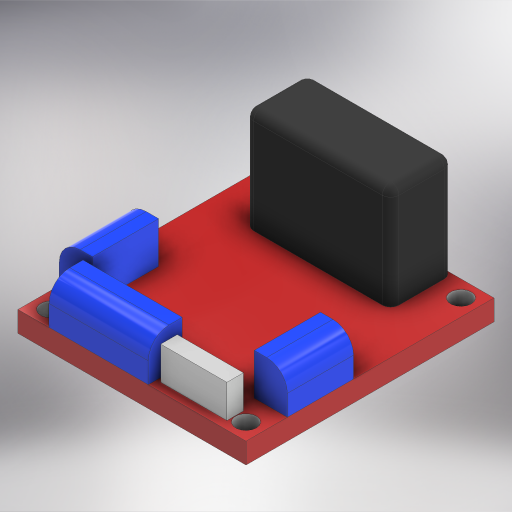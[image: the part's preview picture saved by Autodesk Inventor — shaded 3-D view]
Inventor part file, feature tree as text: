
AUTODESK INVENTOR PART (.ipt)
format: ipt  version: 2024 (Build 280153000, 153)  size: 461,312 bytes
history: native  units: mm
features: other x21, extrude x9, sketch x9, fillet x7
ambient origin geometry x8: Origin, YZ Plane, XZ Plane, XY Plane, X Axis, Y Axis, Z Axis, Center Point
bodies: Body1 (feature_tree)
feature tree (46):
  other  "Sólido1"
  extrude  "Extrusión1"  Depth=55.118mm
  extrude  "Extrusión2"  Depth=10.0mm
  extrude  "Extrusión3"  Depth=15.0mm
  extrude  "Extrusión4"  Depth=10.0mm
  fillet  "Empalme1"  Radius=7.5mm
  fillet  "Empalme2"  Radius=8.0mm
  fillet  "Empalme3"  Radius=16.0mm
  fillet  "Empalme4"  Radius=10.0mm
  fillet  "Empalme5"  Radius=8.0mm
  fillet  "Empalme6"  Radius=24.0mm
  fillet  "Empalme7"  Radius=10.0mm
  extrude  "Extrusión5"  Depth=4.0mm
  extrude  "Extrusión6"  Depth=1.0mm
  extrude  "Extrusión7"  Depth=2.0mm
  extrude  "Extrusión8"  Depth=2.0mm
  extrude  "Extrusión9"  Depth=5.0mm
  sketch  "Boceto1"  dims[d0=59.944mm d1=55.118mm]
  sketch  "Boceto2"  dims[d2=5.0mm d3=0.0mm d4=10.0mm]
  sketch  "Boceto3"  dims[d5=10.0mm d6=15.0mm]
  sketch  "Boceto4"  dims[d7=24.972mm d8=0.0mm d9=10.0mm d10=7.5mm d11=8.0mm d12=16.0mm d13=10.0mm d14=8.0mm d15=24.0mm d16=10.0mm d17=0.0mm]
  sketch  "Boceto6"  dims[d18=2.0mm d19=4.0mm]
  sketch  "Boceto7"  dims[d20=16.0mm d21=1.0mm]
  sketch  "Boceto8"  dims[d22=8.0mm d23=0.0mm d24=2.0mm]
  sketch  "Boceto9"  dims[d25=2.0mm d26=2.0mm]
  sketch  "Boceto10"  dims[d27=2.0mm d28=5.0mm d29=5.0mm d30=5.0mm d31=0.0mm d32=0.001mm d33=0.0mm d34=0.001mm d35=0.0mm d36=0.0mm d37=0.001mm d38=0.0mm d39=0.001mm d40=0.0mm d41=5.0mm d42=4.0mm d43=4.0mm d44=29.972mm d45=27.559mm d46=5.0mm d47=0.0mm]
  other  "Finish1"
  other  "Finish2"
  other  "Finish3"
  other  "Finish4"
  other  "Finish5"
  other  "Finish6"
  other  "Finish7"
  other  "Finish8"
  other  "Finish9"
  other  "Finish10"
  other  "Finish11"
  other  "Finish12"
  other  "Finish13"
  other  "Finish14"
  other  "Finish15"
  other  "Finish16"
  other  "Finish17"
  other  "Finish18"
  other  "Finish19"
  other  "Finish20"
